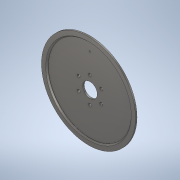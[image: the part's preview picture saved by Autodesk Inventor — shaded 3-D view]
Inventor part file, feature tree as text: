
AUTODESK INVENTOR PART (.ipt)
format: ipt  version: 2021 (Build 250183000, 183)  size: 164,352 bytes
history: native  units: mm
features: extrude x5, sketch x4, chamfer x2, plane x1
ambient origin geometry x8: Origin, YZ Plane, XZ Plane, XY Plane, X Axis, Y Axis, Z Axis, Center Point
bodies: Solid1 (feature_tree)
feature tree (12):
  sketch  "Sketch1"  dims[d0=310.0mm d1=48.0mm]
  extrude  "Extrusion1"  Depth=48.0mm
  extrude  "Extrusion2"  Depth=5.0mm TaperAngle=0.0deg
  extrude  "Extrusion3"  Depth=5.0mm TaperAngle=0.0deg
  chamfer  "Chamfer1"  Distance=3.0mm Angle=45.0deg
  chamfer  "Chamfer2"  Distance=4.0mm Angle=45.0deg
  extrude  "Extrusion4"  Depth=10.0mm
  sketch  "Sketch3"  dims[d5=5.0mm d6=0.0mm d7=5.0mm d8=0.0mm d9=3.0mm d10=2.0mm d11=45.0deg d12=4.0mm d13=2.0mm d14=45.0deg]
  plane  "Work Plane1"
  extrude  "Extrusion6"  Depth=10.0mm TaperAngle=360.0deg
  sketch  "Sketch2"  dims[d2=274.0mm d3=5.0mm d4=0.0mm]
  sketch  "Sketch5"  dims[d17=10.0mm d18=43.0mm d19=60.0mm d21=360.0deg d23=5.0mm d24=0.0mm d27=0.0mm d31=5.0mm d32=45.0mm d33=10.0mm d34=0.0mm]
